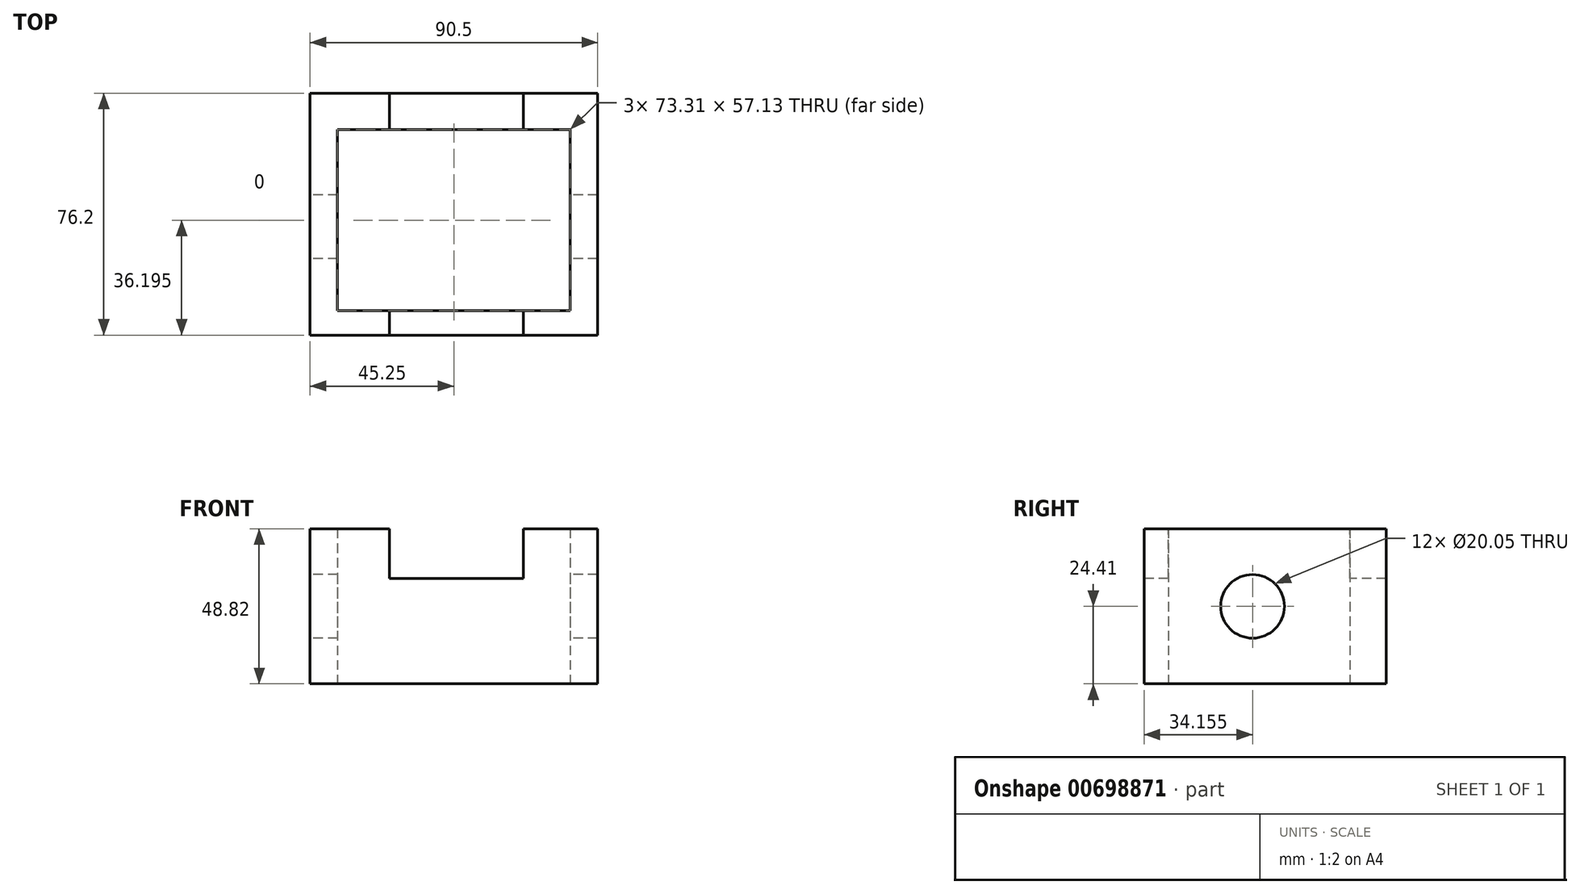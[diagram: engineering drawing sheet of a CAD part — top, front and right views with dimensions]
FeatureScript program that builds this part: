
annotation { "Feature Type Name" : "Feature", "Feature Type Description" : "" }
export const myFeature = defineFeature(function(context is Context, id is Id, definition is map)
    precondition{}
    {
        {
            var Q0;
            Q0=qCreatedBy(makeId("Front.planeOp"),FACE);
            var sketch = newSketch(context, id + "F0", { "sketchPlane" : qUnion([Q0])});
            skLineSegment(sketch, "E0.bottom", {"start": v(-45.25, 24.41) * mm, "end": v(45.25, 24.41) * mm});
            skLineSegment(sketch, "E0.top", {"start": v(-45.25, -24.41) * mm, "end": v(45.25, -24.41) * mm});
            skLineSegment(sketch, "E0.left", {"start": v(-45.25, 24.41) * mm, "end": v(-45.25, -24.41) * mm});
            skLineSegment(sketch, "E0.right", {"start": v(45.25, 24.41) * mm, "end": v(45.25, -24.41) * mm});
            skPoint(sketch, "E0.middle", {"position": v(0, 0) * mm});
            skSolve(sketch);
        }
        {
            var Q0;
            Q0=makeQuery(id+"F0.imprint","IMPRINT",FACE,{"disambiguationData":[TD([[makeQuery(id+"F0.imprint","IMPRINT",EDGE,{"derivedFrom":sQuery(id+"F0.wireOp",EDGE,"E0.bottom")}),-1.0]])]});
            extrude(context, id + "F1", {"entities" : qUnion([Q0]), "depth" : 76.2 * mm, "offsetDistance" : 25.4 * mm});
        }
        {
            var Q0;
            Q0=makeQuery(id+"F1.opExtrude","SWEPT_FACE",FACE,{"disambiguationData":[OSD([sQuery(id+"F0.wireOp",EDGE,"E0.top")])]});
            var sketch = newSketch(context, id + "F2", { "sketchPlane" : qUnion([Q0])});
            skLineSegment(sketch, "E1.bottom", {"start": v(-36.65, 68.57) * mm, "end": v(36.65, 68.57) * mm});
            skLineSegment(sketch, "E1.top", {"start": v(-36.65, 11.44) * mm, "end": v(36.65, 11.44) * mm});
            skLineSegment(sketch, "E1.left", {"start": v(-36.65, 68.57) * mm, "end": v(-36.65, 11.44) * mm});
            skLineSegment(sketch, "E1.right", {"start": v(36.65, 68.57) * mm, "end": v(36.65, 11.44) * mm});
            skPoint(sketch, "E1.middle", {"position": v(0, 40) * mm});
            skSolve(sketch);
        }
        {
            var Q0;
            Q0=makeQuery(id+"F2.imprint","IMPRINT",FACE,{"disambiguationData":[TD([[makeQuery(id+"F2.imprint","IMPRINT",EDGE,{"derivedFrom":sQuery(id+"F2.wireOp",EDGE,"E1.bottom")}),-1.0]])]});
            extrude(context, id + "F3", {"entities" : qUnion([Q0]), "operationType" : NewBodyOperationType.REMOVE, "oppositeDirection" : true, "depth" : 76.2 * mm, "offsetDistance" : 25.4 * mm});
        }
        {
            var Q0;
            Q0=makeQuery(id+"F1.opExtrude","SWEPT_FACE",FACE,{"disambiguationData":[OSD([sQuery(id+"F0.wireOp",EDGE,"E0.left")])]});
            var sketch = newSketch(context, id + "F4", { "sketchPlane" : qUnion([Q0])});
            skCircle(sketch, "E2", {"center": v(42.05, 0) * mm, "radius": 10.02 * mm});
            skSolve(sketch);
        }
        {
            var Q0;
            Q0=makeQuery(id+"F4.imprint","IMPRINT",FACE,{"disambiguationData":[TD([[makeQuery(id+"F4.imprint","IMPRINT",EDGE,{"derivedFrom":sQuery(id+"F4.wireOp",EDGE,"E2")}),1.0]])]});
            extrude(context, id + "F5", {"entities" : qUnion([Q0]), "operationType" : NewBodyOperationType.REMOVE, "oppositeDirection" : true, "depth" : 101.6 * mm, "offsetDistance" : 25.4 * mm});
        }
        {
            var Q0;
            Q0=makeQuery(id+"F1.opExtrude","CAP_FACE",FACE,{"disambiguationData":[OSD([sQuery(id+"F0.wireOp",EDGE,"E0.bottom"),sQuery(id+"F0.wireOp",EDGE,"E0.top"),sQuery(id+"F0.wireOp",EDGE,"E0.left"),sQuery(id+"F0.wireOp",EDGE,"E0.right")])],"isStart":false});
            var sketch = newSketch(context, id + "F6", { "sketchPlane" : qUnion([Q0])});
            skLineSegment(sketch, "E3.bottom", {"start": v(-20.33, 24.41) * mm, "end": v(21.93, 24.41) * mm});
            skLineSegment(sketch, "E3.top", {"start": v(-20.33, 8.82) * mm, "end": v(21.93, 8.82) * mm});
            skLineSegment(sketch, "E3.left", {"start": v(-20.33, 24.41) * mm, "end": v(-20.33, 8.82) * mm});
            skLineSegment(sketch, "E3.right", {"start": v(21.93, 24.41) * mm, "end": v(21.93, 8.82) * mm});
            skSolve(sketch);
        }
        {
            var Q0;
            Q0=makeQuery(id+"F6.imprint","IMPRINT",FACE,{"disambiguationData":[TD([[makeQuery(id+"F6.imprint","IMPRINT",EDGE,{"derivedFrom":sQuery(id+"F6.wireOp",EDGE,"E3.bottom")}),-1.0]])]});
            extrude(context, id + "F7", {"entities" : qUnion([Q0]), "operationType" : NewBodyOperationType.REMOVE, "oppositeDirection" : true, "depth" : 101.6 * mm, "offsetDistance" : 25.4 * mm});
        }
    });
